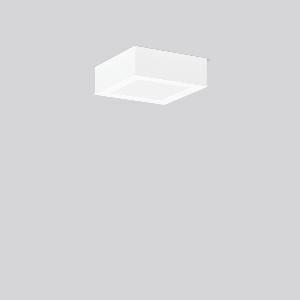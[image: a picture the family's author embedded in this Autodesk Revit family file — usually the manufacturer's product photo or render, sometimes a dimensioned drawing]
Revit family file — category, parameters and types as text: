
# Revit family: toledo_flat_square_a_901552_002_1_0ad4
name_source: partatom
category: Lighting Fixtures
units: mm (PartAtom-declared; Revit-internal decimal feet)

## family parameters
Cut with Voids When Loaded = No
Host = Face
Light Source = No
Part Type = Normal
Room Calculation Point = No
Round Connector Dimension = Use Diameter
Shared = No

## types (1)
- TOLEDO FLAT square A (1 x LED Modul 840, 800 lm, 4000)
    Apparent Load = 8 VA
    CIE Flux Codes = 49 80 96 100 100
    Color Rendering = 80
    Color Temperature = 4000
    Default Elevation = 1800 mm
    Description = Series: TOLEDO FLAT square
Ultra thin surface mounted downlight. Surface mounted housing: sheet steel, powder-coated. Square cover plate: die-cast aluminium, powder coated. Light guide and diffuser made of non-yellowing PMMA, opal matt. Suitable for Ceiling mounting, Wall (surface). Driver integrated. 
Colour: white
Length: 172 mm
Width: 172 mm
Height: 58 mm
Lamp: LED
Socket: without socket
Colour temperature: 4000K
Colour rendering index (CRI): 80
System power: 8 W
Rated luminous flux: 800 lm
Luminous efficiency: 100 lm/W
Control gear: Regulated power supply
Protection class: II
Type of protection: IP 40
    Height = 58 mm
    Lamp = 1 x LED Modul 840
    Lamp Light Flux = 800 lm
    Lamp count = 1
    Length = 172 mm
    Lifetime = 50000 h
    Luminous efficacy = 100 lm/W
    Manufacturer = RZB
    ModVariant = No
    Model = 901552.002.1
    Mounting Place = Ceiling
    Mounting Type = Surface mounted
    Number of Poles = 1
    OnlyDefault = Yes
    Power Factor = 1
    Product Name = TOLEDO FLAT square A
    Product group = Surface mounted downlights
    ProductGroupID = 302
    Protection Class = Protection class II
    Protection Degree = IP 40
    RLX_Detail_Level = 1
    RLX_Emergency_Light_Flux = 0 lm
    RLX_Emergency_Type = 0
    RLX_Emergency_Type_DB = No
    RlxData = <blob elided: 13705 chars, md5=85678e1b>
    Socket = socket
    Standby Power = 0 W
    System Light Flux = 800 lm
    System Power = 8 W
    Type Comments = Product without accessories
    Type Image = 901552.002.jpg
    URL = http://relux.com
    VarID = ---
    Voltage = 230 V
    Voltage Range = 220-240 V
    Weight = 0.00 kg
    Width = 172 mm

## geometry (parser evidence)
native form markers: Sweep x8
no freeform markers — native parametric forms only
